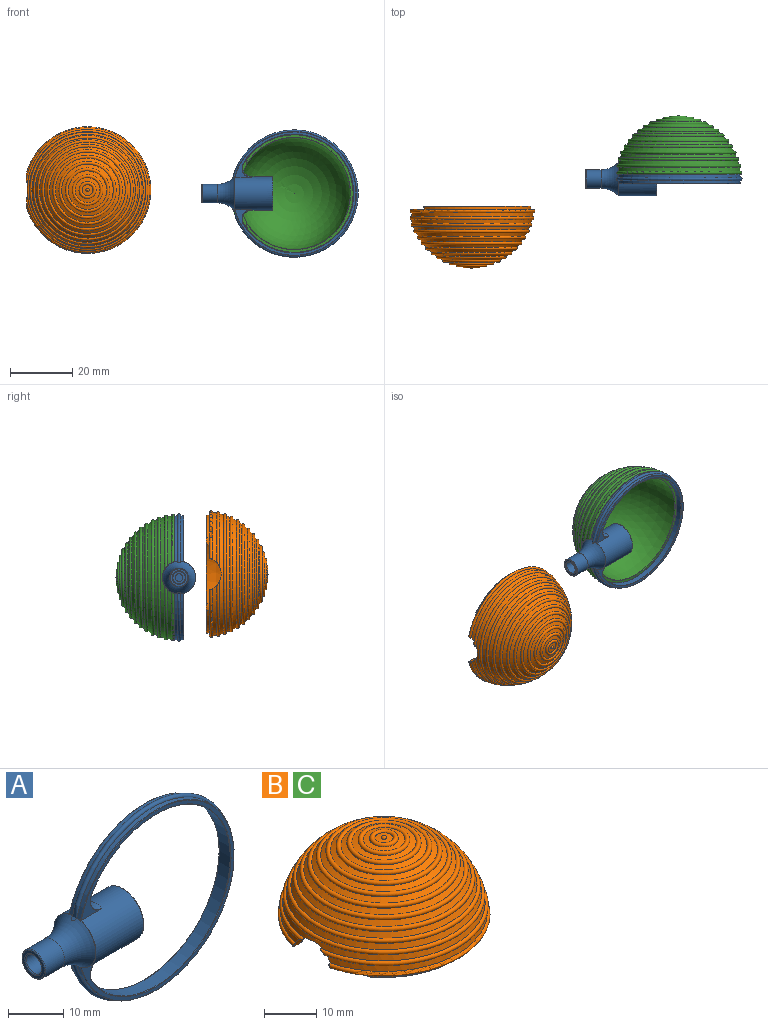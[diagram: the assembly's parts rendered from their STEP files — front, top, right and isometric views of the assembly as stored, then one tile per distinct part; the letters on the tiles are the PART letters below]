
ASSEMBLY  parts=3 mates=1
PART A: 34 faces, bbox 52.7x23.6x44.4 mm
  f0: plane 0.89x0.16mm, normal (0.26,0,-0.97), area 0mm2, adj f1,f4,f18,f30
  f1: sphere r=20mm, area 104.5mm2, adj f0,f2,f18,f28,f30
  f2: plane 0.89x0.16mm, normal (0.26,0,0.97), area 0mm2, adj f1,f4,f18,f30
  f3: plane 0.89x0.16mm, normal (0.26,0,-0.97), area 0mm2, adj f4,f16,f18,f29
  f4: torus R=10.9mm, axis (1,0,0), area 146.6mm2, adj f0,f2,f3,f13,f17,f18,f29,f30
  f5: plane 39.7x39.03mm, normal (0,-1,0), area 94.4mm2, adj f12,f24,f25,f26,f27
  f6: plane 39.7x39.03mm, normal (0,1,0), area 94.4mm2, adj f12,f21,f22,f23,f28
  f7: cylinder r=2mm len=10.8mm, axis (1,0,0), area 135.7mm2, adj f8,f33
  f8: plane 4x4mm, normal (-1,0,0), area 7.7mm2, adj f7,f9
  f9: cylinder r=1.25mm len=10mm, axis (1,0,0), area 78.5mm2, adj f8,f10
  f10: plane 2.5x2.5mm, normal (-1,0,0), area 4.9mm2, adj f9
  f11: plane 10.3x10.3mm, normal (1,0,0), area 83.3mm2, adj f31
  f12: cylinder r=5.35mm len=12.14mm, axis (1,0,0), area 374.5mm2, adj f5,f6,f19,f20,f21,f23,f24,f26
  f13: cylinder r=3mm len=6mm, axis (1,0,0), area 90.5mm2, adj f4,f32
  f14: plane 5.6x5.6mm, normal (-1,0,0), area 9.4mm2, adj f32,f33
  f15: cylinder r=19mm len=38mm, axis (0,1,0), area 276.2mm2, adj f19,f20,f22,f25
  f16: sphere r=20mm, area 104.5mm2, adj f3,f17,f18,f27,f29
  f17: plane 0.89x0.16mm, normal (0.26,0,0.97), area 0mm2, adj f4,f16,f18,f29
  f18: torus R=20mm, axis (0,1,0), area 186.3mm2, adj f0,f1,f2,f3,f4,f16,f17
  f19: bspline ~6.46x5.36mm, area 16mm2, adj f12,f15,f21,f24
  f20: bspline ~6.46x5.36mm, area 16mm2, adj f12,f15,f23,f26
  f21: bspline ~5.12x3.51mm, area 0.8mm2, adj f6,f12,f19,f22
  f22: torus R=19.1mm, axis (0,-1,0), area 15.6mm2, adj f6,f15,f21,f23
  f23: bspline ~5.12x3.51mm, area 0.8mm2, adj f6,f12,f20,f22
  f24: bspline ~5.12x3.51mm, area 0.8mm2, adj f5,f12,f19,f25
  f25: torus R=19.1mm, axis (0,-1,0), area 15.6mm2, adj f5,f15,f24,f26
  f26: bspline ~5.12x3.51mm, area 0.8mm2, adj f5,f12,f20,f25
  f27: torus R=19.85mm, axis (0,-1,0), area 17.2mm2, adj f5,f12,f16,f29
  f28: torus R=19.85mm, axis (0,-1,0), area 17.2mm2, adj f1,f6,f12,f30
  f29: torus R=5.25mm, axis (-1,0,0), area 1.1mm2, adj f3,f4,f12,f16,f17,f27
  f30: torus R=5.25mm, axis (-1,0,0), area 1.1mm2, adj f0,f1,f2,f4,f12,f28
  f31: torus R=5.15mm, axis (-1,0,0), area 10.4mm2, adj f11,f12
  f32: torus R=2.8mm, axis (-1,0,0), area 5.8mm2, adj f13,f14
  f33: torus R=2.2mm, axis (-1,0,0), area 4.1mm2, adj f7,f14
PART B: 51 faces, bbox 43.6x44.1x20 mm
  f0: plane 37.8x34.22mm, normal (0,0,-1), area 76.1mm2, adj f45,f47,f49,f50
  f1: sphere r=20mm, area 39.8mm2, adj f38,f41
  f2: sphere r=20mm, area 64mm2, adj f36,f39
  f3: sphere r=20mm, area 87.3mm2, adj f34,f37
  f4: sphere r=20mm, area 109.6mm2, adj f32,f35
  f5: sphere r=20mm, area 130.4mm2, adj f30,f33
  f6: sphere r=20mm, area 149.6mm2, adj f28,f31
  f7: sphere r=20mm, area 166.9mm2, adj f26,f29
  f8: sphere r=20mm, area 182mm2, adj f24,f27
  f9: sphere r=20mm, area 194.9mm2, adj f22,f25
  f10: sphere r=20mm, area 205.3mm2, adj f20,f23
  f11: sphere r=20mm, area 208.4mm2, adj f18,f21,f44
  f12: sphere r=20mm, area 202.5mm2, adj f16,f19,f44
  f13: sphere r=18mm, area 1919.4mm2, adj f14,f45,f46,f49,f50
  f14: plane 39.68x39.01mm, normal (0,0,-1), area 105.8mm2, adj f13,f15,f44,f46,f48,f49,f50
  f15: cylinder r=19mm len=38mm, axis (0,0,-1), area 84.9mm2, adj f14,f47,f49,f50
  f16: cylinder r=19.89mm len=39.78mm, axis (0,0,-1), area 57.6mm2, adj f12,f17,f44
  f17: torus R=19.89mm, axis (0,0,-1), area 178.6mm2, adj f16,f44,f48
  f18: cone r=19.47mm half-angle=6.5deg, axis (0,0,-1), area 58.5mm2, adj f11,f19,f44
  f19: torus R=19.53mm, axis (0,0,-1), area 180.9mm2, adj f12,f18,f44
  f20: cone r=18.81mm half-angle=12.9deg, axis (0,0,-1), area 59.3mm2, adj f10,f21
  f21: torus R=18.92mm, axis (0,0,-1), area 184.3mm2, adj f11,f20
  f22: cone r=17.9mm half-angle=19.4deg, axis (0,0,-1), area 56.5mm2, adj f9,f23
  f23: torus R=18.07mm, axis (0,0,-1), area 176mm2, adj f10,f22
  f24: cone r=16.77mm half-angle=25.8deg, axis (0,0,-1), area 53mm2, adj f8,f25
  f25: torus R=16.99mm, axis (0,0,-1), area 165.5mm2, adj f9,f24
  f26: cone r=15.43mm half-angle=32.3deg, axis (0,0,-1), area 48.9mm2, adj f7,f27
  f27: torus R=15.69mm, axis (0,0,-1), area 152.9mm2, adj f8,f26
  f28: cone r=13.89mm half-angle=38.8deg, axis (0,0,-1), area 44.1mm2, adj f6,f29
  f29: torus R=14.2mm, axis (0,0,-1), area 138.4mm2, adj f7,f28
  f30: cone r=12.17mm half-angle=45.2deg, axis (0,0,-1), area 38.8mm2, adj f5,f31
  f31: torus R=12.52mm, axis (0,0,-1), area 122.1mm2, adj f6,f30
  f32: cone r=10.3mm half-angle=51.7deg, axis (0,0,-1), area 33mm2, adj f4,f33
  f33: torus R=10.69mm, axis (0,0,-1), area 104.2mm2, adj f5,f32
  f34: cone r=8.29mm half-angle=58.2deg, axis (0,0,-1), area 26.7mm2, adj f3,f35
  f35: torus R=8.72mm, axis (0,0,-1), area 85.1mm2, adj f4,f34
  f36: cone r=6.19mm half-angle=64.6deg, axis (0,0,-1), area 20.1mm2, adj f2,f37
  f37: torus R=6.64mm, axis (0,0,-1), area 64.8mm2, adj f3,f36
  f38: cone r=4mm half-angle=71.1deg, axis (0,0,-1), area 13.3mm2, adj f1,f39
  f39: torus R=4.47mm, axis (0,0,-1), area 43.7mm2, adj f2,f38
  f40: cone r=1.76mm half-angle=77.5deg, axis (0,0,-1), area 6.3mm2, adj f41,f42
  f41: torus R=2.25mm, axis (0,0,-1), area 22.1mm2, adj f1,f40
  f42: sphere r=20mm, area 15.2mm2, adj f40,f43
  f43: sphere r=0.5mm, area 1.6mm2, adj f42
  f44: cylinder r=5.35mm len=10.27mm, axis (1,0,0), area 29.9mm2, adj f11,f12,f14,f16,f17,f18,f19,f46
  f45: torus R=18.09mm, axis (0,0,1), area 14.3mm2, adj f0,f13,f49,f50
  f46: torus R=5.45mm, axis (1,0,0), area 1.8mm2, adj f13,f14,f44
  f47: torus R=18.9mm, axis (0,0,1), area 14.8mm2, adj f0,f15,f49,f50
  f48: torus R=19.84mm, axis (0,0,-1), area 17.2mm2, adj f14,f17,f44
  f49: cylinder r=6mm len=2.28mm, axis (0,0,-1), area 2.2mm2, adj f0,f13,f14,f15,f45,f47
  f50: cylinder r=6mm len=2.28mm, axis (0,0,-1), area 2.2mm2, adj f0,f13,f14,f15,f45,f47
PART C: same geometry as B
PLACE A rot(axis=(1,0,0),180deg) t=(-15.91,-144.43,80.29)mm
PLACE B rot(axis=(1,0,0),90deg) t=(-82.47,-152.67,81.4)mm
PLACE C rot(axis=(-1,0,0),90deg) t=(-15.91,-144.53,80.29)mm
MATE fastened C.f15 <-> A.f27  axis (0,-1,0) through (-15.91,-143.03,80.29)mm
